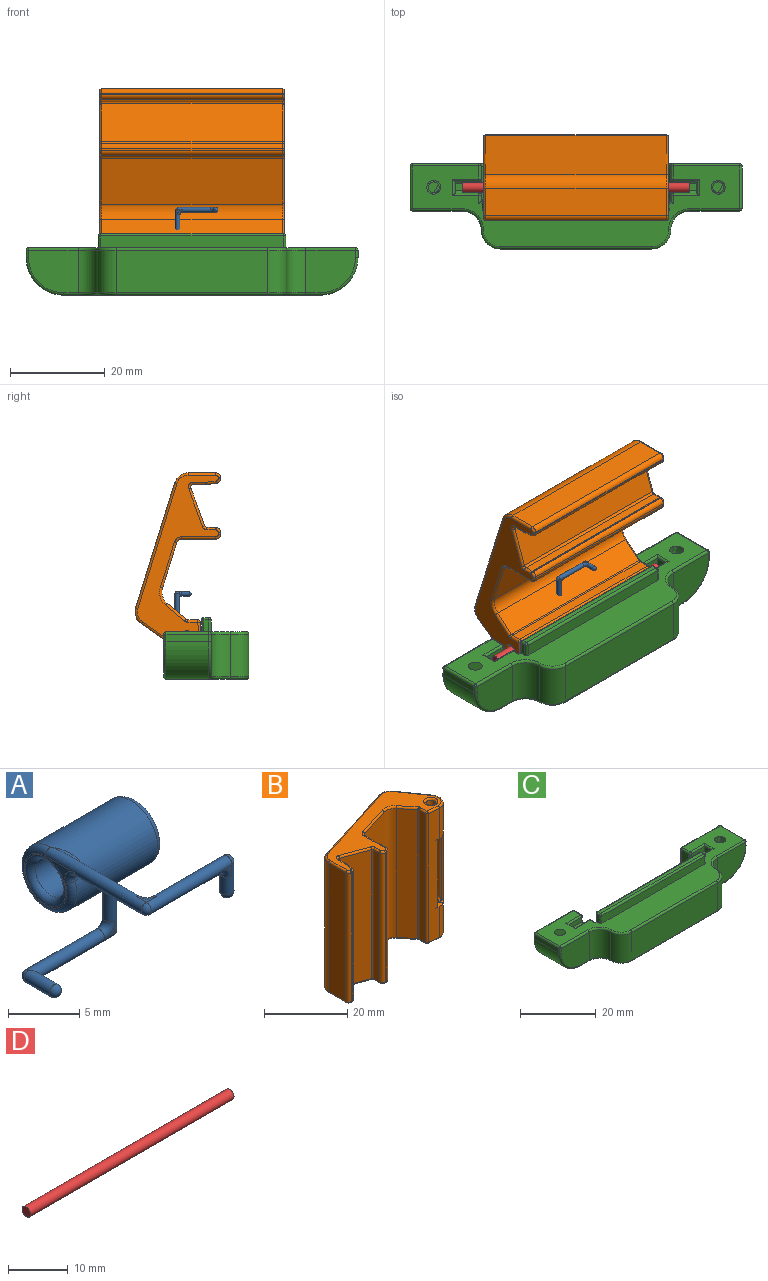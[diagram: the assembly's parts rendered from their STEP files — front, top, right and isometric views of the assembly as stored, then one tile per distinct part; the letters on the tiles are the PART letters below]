
ASSEMBLY  parts=4 mates=3
PART A: 33 faces, bbox 9x12.8x12.8 mm
  f0: plane 1x1mm, normal (0,0,1), area 0.2mm2, adj f12,f14,f16
  f1: plane 1x1mm, normal (0,1,0), area 0.2mm2, adj f24,f27,f29
  f2: plane 1x1mm, normal (0,1,0), area 0.2mm2, adj f16,f19,f20
  f3: cylinder r=2.62mm len=8mm, axis (-1,0,0), area 127.7mm2, adj f10,f11,f21,f22
  f4: cylinder r=1.5mm len=8mm, axis (-1,0,0), area 75.4mm2, adj f31,f32
  f5: plane 5.04x4.25mm, normal (1,0,0), area 2.5mm2, adj f21,f23,f24,f32
  f6: plane 5.04x4.25mm, normal (-1,0,0), area 2.5mm2, adj f11,f12,f13,f31
  f7: plane 1x1mm, normal (0,0,-1), area 0.2mm2, adj f12,f14,f16
  f8: plane 1x1mm, normal (0,-1,0), area 0.2mm2, adj f16,f19,f20
  f9: plane 1x1mm, normal (0,-1,0), area 0.2mm2, adj f24,f27,f29
  f10: bspline ~2.92x1.68mm, area 1.9mm2, adj f3,f12,f13
  f11: torus R=2.12mm, axis (1,0,0), area 9.7mm2, adj f3,f6,f12,f13
  f12: cylinder r=0.5mm len=9.5mm, axis (0,1,0), area 22.9mm2, adj f0,f6,f7,f10,f11,f13,f14,f15
  f13: torus R=1mm, axis (1,0,0), area 1mm2, adj f6,f10,f11,f12
  f14: torus R=1mm, axis (0,0,-1), area 1.7mm2, adj f0,f7,f12,f16
  f15: sphere r=0.5mm, area 0.8mm2, adj f12,f16
  f16: cylinder r=0.5mm len=8mm, axis (1,0,0), area 22mm2, adj f0,f2,f7,f8,f14,f15,f17,f20
  f17: sphere r=0.5mm, area 0.8mm2, adj f16,f19
  f18: sphere r=0.5mm, area 1.6mm2, adj f19
  f19: cylinder r=0.5mm len=2.5mm, axis (0,0,-1), area 6.3mm2, adj f2,f8,f17,f18,f20
  f20: torus R=1mm, axis (0,1,0), area 1.7mm2, adj f2,f8,f16,f19
  f21: torus R=2.12mm, axis (1,0,0), area 9.7mm2, adj f3,f5,f23,f24
  f22: bspline ~2.92x1.68mm, area 1.9mm2, adj f3,f23,f24
  f23: torus R=1mm, axis (1,0,0), area 1mm2, adj f5,f21,f22,f24
  f24: cylinder r=0.5mm len=9.5mm, axis (0,0,-1), area 22.9mm2, adj f1,f5,f9,f21,f22,f23,f26,f27
  f25: sphere r=0.5mm, area 0.8mm2, adj f29,f30
  f26: sphere r=0.5mm, area 0.8mm2, adj f24,f29
  f27: torus R=1mm, axis (0,1,0), area 1.7mm2, adj f1,f9,f24,f29
  f28: sphere r=0.5mm, area 1.6mm2, adj f30
  f29: cylinder r=0.5mm len=8mm, axis (-1,0,0), area 23.1mm2, adj f1,f9,f25,f26,f27,f30
  f30: cylinder r=0.5mm len=2.5mm, axis (0,1,0), area 7.4mm2, adj f25,f28,f29
  f31: torus R=2mm, axis (1,0,0), area 8.3mm2, adj f4,f6
  f32: torus R=2mm, axis (1,0,0), area 8.3mm2, adj f4,f5
PART B: 166 faces, bbox 38.6x18.5x39.2 mm
  f0: plane 19x5.92mm, normal (0.82,0.57,0), area 115.5mm2, adj f27,f32,f34,f35,f37,f39,f40,f42
  f1: plane 9x8.03mm, normal (0.82,0.57,0), area 88.3mm2, adj f3,f4,f30,f117
  f2: cylinder r=1.2mm len=8.5mm, axis (0,0,-1), area 64.1mm2, adj f162,f164
  f3: cylinder r=3mm len=38mm, axis (0,0,-1), area 109.9mm2, adj f1,f5,f6,f27,f30,f31,f63,f83
  f4: cylinder r=3mm len=38mm, axis (0,0,-1), area 212.1mm2, adj f1,f5,f26,f29,f30,f31,f86,f87
  f5: plane 9x8.03mm, normal (0.82,0.57,0), area 88.3mm2, adj f3,f4,f31,f139
  f6: plane 38x26.38mm, normal (-0.3,0.95,0), area 1050mm2, adj f3,f23,f113,f143
  f7: plane 38x5.79mm, normal (-1,0,0), area 220.2mm2, adj f23,f61,f109,f147
  f8: plane 38x0.22mm, normal (0,-1,0), area 8.5mm2, adj f59,f61,f105,f151
  f9: plane 38x2.07mm, normal (0.99,-0.13,0), area 79.2mm2, adj f59,f60,f101,f155
  f10: plane 38x2.72mm, normal (1,0,0), area 103.3mm2, adj f60,f94,f100,f159
  f11: plane 38x8mm, normal (-0.34,-0.94,0), area 323.5mm2, adj f93,f94,f104,f160
  f12: plane 38x1.78mm, normal (-1,0,0), area 67.5mm2, adj f56,f93,f108,f156
  f13: plane 38x0.1mm, normal (-0.98,-0.2,0), area 3.8mm2, adj f56,f57,f112,f152
  f14: plane 38x0.48mm, normal (0,-1,0), area 18.2mm2, adj f57,f58,f116,f148
  f15: plane 38x7.26mm, normal (1,0,0), area 276.1mm2, adj f55,f58,f120,f144
  f16: plane 38x9.6mm, normal (0.3,-0.95,0), area 382mm2, adj f24,f55,f124,f140
  f17: plane 38x4.06mm, normal (-0.77,-0.64,0), area 201.4mm2, adj f24,f128,f132,f136
  f18: plane 38x2.09mm, normal (-1,0,0), area 79.5mm2, adj f92,f127,f131,f132
  f19: cylinder r=1.2mm len=8.5mm, axis (0,0,-1), area 64.1mm2, adj f163,f165
  f20: plane 38x3.51mm, normal (-0.09,-1,0), area 123.7mm2, adj f28,f30,f31,f86,f92,f95,f123,f133
  f21: plane 37x17.03mm, normal (0,0,1), area 195.9mm2, adj f131,f133,f134,f136,f137,f138,f139,f140
  f22: plane 37x17.03mm, normal (0,0,-1), area 195.9mm2, adj f99,f100,f101,f102,f103,f104,f105,f106
  f23: cylinder r=3mm len=38mm, axis (0,0,1), area 144.6mm2, adj f6,f7,f111,f145
  f24: cylinder r=3mm len=38mm, axis (0,0,-1), area 134mm2, adj f16,f17,f126,f138
  f25: cylinder r=2.5mm len=19.5mm, axis (0,0,1), area 76.8mm2, adj f26,f29,f31,f87,f88,f90
  f26: plane 19x0.35mm, normal (-0.71,0.71,0), area 9.5mm2, adj f4,f25,f88,f89
  f27: plane 19x1.2mm, normal (1,-0.08,0), area 23mm2, adj f0,f3,f33,f38,f43,f49,f52,f63
  f28: cylinder r=3mm len=20mm, axis (0,0,1), area 163.3mm2, adj f20,f30,f31,f96,f97,f98
  f29: plane 19x0.35mm, normal (-0.71,-0.71,0), area 9.5mm2, adj f4,f25,f87,f91
  f30: plane 13.71x11.01mm, normal (0,0,1), area 35.3mm2, adj f1,f3,f4,f20,f28,f50,f63,f64
  f31: plane 13.71x11.05mm, normal (0,0,-1), area 37.5mm2, adj f3,f4,f5,f20,f25,f28,f54,f81
  f32: plane 5.53x4.92mm, normal (0,0,1), area 12.5mm2, adj f0,f36,f68,f71
  f33: plane 4.1x2.87mm, normal (0.57,-0.82,0), area 2.5mm2, adj f27,f36,f70,f71
  f34: plane 5.53x4.92mm, normal (0,0,-1), area 12.5mm2, adj f0,f36,f69,f70
  f35: plane 4.1x2.87mm, normal (-0.57,0.82,0), area 2.5mm2, adj f0,f36,f68,f69
  f36: plane 2.87x2.01mm, normal (0.82,0.57,0), area 5mm2, adj f32,f33,f34,f35,f68,f69,f70,f71
  f37: plane 5.53x4.92mm, normal (0,0,1), area 12.5mm2, adj f0,f41,f72,f75
  f38: plane 4.1x2.87mm, normal (0.57,-0.82,0), area 2.5mm2, adj f27,f41,f74,f75
  f39: plane 5.53x4.92mm, normal (0,0,-1), area 12.5mm2, adj f0,f41,f73,f74
  f40: plane 4.1x2.87mm, normal (-0.57,0.82,0), area 2.5mm2, adj f0,f41,f72,f73
  f41: plane 2.87x2.01mm, normal (0.82,0.57,0), area 5mm2, adj f37,f38,f39,f40,f72,f73,f74,f75
  f42: plane 5.53x4.92mm, normal (0,0,1), area 12.5mm2, adj f0,f46,f76,f79
  f43: plane 4.1x2.87mm, normal (0.57,-0.82,0), area 2.5mm2, adj f27,f46,f76,f77
  f44: plane 5.53x4.92mm, normal (0,0,-1), area 12.5mm2, adj f0,f46,f77,f78
  f45: plane 4.1x2.87mm, normal (-0.57,0.82,0), area 2.5mm2, adj f0,f46,f78,f79
  f46: plane 2.87x2.01mm, normal (0.82,0.57,0), area 5mm2, adj f42,f43,f44,f45,f76,f77,f78,f79
  f47: plane 5.53x4.92mm, normal (0,0,-1), area 12.5mm2, adj f0,f50,f62,f67
  f48: plane 4.1x2.87mm, normal (-0.57,0.82,0), area 2.5mm2, adj f0,f50,f66,f67
  f49: plane 4.1x2.87mm, normal (0.57,-0.82,0), area 2.5mm2, adj f27,f50,f62,f64
  f50: plane 2.87x2.01mm, normal (0.82,0.57,0), area 5mm2, adj f30,f47,f48,f49,f62,f64,f66,f67
  f51: plane 5.53x4.92mm, normal (0,0,1), area 12.5mm2, adj f0,f54,f80,f85
  f52: plane 4.1x2.87mm, normal (0.57,-0.82,0), area 2.5mm2, adj f27,f54,f84,f85
  f53: plane 4.1x2.87mm, normal (-0.57,0.82,0), area 2.5mm2, adj f0,f54,f80,f82
  f54: plane 2.87x2.01mm, normal (0.82,0.57,0), area 5mm2, adj f31,f51,f52,f53,f80,f82,f84,f85
  f55: cylinder r=1mm len=38mm, axis (0,0,1), area 48.2mm2, adj f15,f16,f122,f142
  f56: cylinder r=1mm len=38mm, axis (0,0,-1), area 7.5mm2, adj f12,f13,f110,f154
  f57: cylinder r=1mm len=38mm, axis (0,0,-1), area 52.2mm2, adj f13,f14,f114,f150
  f58: cylinder r=1mm len=38mm, axis (0,0,-1), area 59.7mm2, adj f14,f15,f118,f146
  f59: cylinder r=1mm len=38mm, axis (0,0,-1), area 54.7mm2, adj f8,f9,f103,f153
  f60: cylinder r=1mm len=38mm, axis (0,0,1), area 5mm2, adj f9,f10,f99,f157
  f61: cylinder r=1mm len=38mm, axis (0,0,-1), area 59.7mm2, adj f7,f8,f107,f149
  f62: cylinder r=0.5mm len=4.38mm, axis (-0.82,-0.57,0), area 3.9mm2, adj f0,f47,f49,f50
  f63: cylinder r=0.5mm len=1.48mm, axis (-0.08,-1,0), area 1mm2, adj f3,f27,f30,f64
  f64: cylinder r=0.5mm len=4.57mm, axis (0.82,0.57,0), area 4mm2, adj f30,f49,f50,f63
  f65: cylinder r=0.5mm len=4.23mm, axis (0.57,-0.82,0), area 3.4mm2, adj f0,f30,f66,f98
  f66: cylinder r=0.5mm len=4.79mm, axis (0.82,0.57,0), area 4.1mm2, adj f30,f48,f50,f65
  f67: cylinder r=0.5mm len=4.38mm, axis (-0.82,-0.57,0), area 3.9mm2, adj f0,f47,f48,f50
  f68: cylinder r=0.5mm len=4.38mm, axis (0.82,0.57,0), area 3.9mm2, adj f0,f32,f35,f36
  f69: cylinder r=0.5mm len=4.38mm, axis (-0.82,-0.57,0), area 3.9mm2, adj f0,f34,f35,f36
  f70: cylinder r=0.5mm len=4.38mm, axis (-0.82,-0.57,0), area 3.9mm2, adj f0,f33,f34,f36
  f71: cylinder r=0.5mm len=4.38mm, axis (0.82,0.57,0), area 3.9mm2, adj f0,f32,f33,f36
  f72: cylinder r=0.5mm len=4.38mm, axis (0.82,0.57,0), area 3.9mm2, adj f0,f37,f40,f41
  f73: cylinder r=0.5mm len=4.38mm, axis (-0.82,-0.57,0), area 3.9mm2, adj f0,f39,f40,f41
  f74: cylinder r=0.5mm len=4.38mm, axis (-0.82,-0.57,0), area 3.9mm2, adj f0,f38,f39,f41
  f75: cylinder r=0.5mm len=4.38mm, axis (0.82,0.57,0), area 3.9mm2, adj f0,f37,f38,f41
  f76: cylinder r=0.5mm len=4.38mm, axis (0.82,0.57,0), area 3.9mm2, adj f0,f42,f43,f46
  f77: cylinder r=0.5mm len=4.38mm, axis (-0.82,-0.57,0), area 3.9mm2, adj f0,f43,f44,f46
  f78: cylinder r=0.5mm len=4.38mm, axis (-0.82,-0.57,0), area 3.9mm2, adj f0,f44,f45,f46
  f79: cylinder r=0.5mm len=4.38mm, axis (0.82,0.57,0), area 3.9mm2, adj f0,f42,f45,f46
  f80: cylinder r=0.5mm len=4.38mm, axis (0.82,0.57,0), area 3.9mm2, adj f0,f51,f53,f54
  f81: cylinder r=0.5mm len=4.23mm, axis (-0.57,0.82,0), area 3.4mm2, adj f0,f31,f82,f96
  f82: cylinder r=0.5mm len=4.79mm, axis (-0.82,-0.57,0), area 4.1mm2, adj f31,f53,f54,f81
  f83: cylinder r=0.5mm len=1.48mm, axis (0.08,1,0), area 1mm2, adj f3,f27,f31,f84
  f84: cylinder r=0.5mm len=4.57mm, axis (-0.82,-0.57,0), area 4mm2, adj f31,f52,f54,f83
  f85: cylinder r=0.5mm len=4.38mm, axis (0.82,0.57,0), area 3.9mm2, adj f0,f51,f52,f54
  f86: cylinder r=0.5mm len=9mm, axis (0,0,-1), area 0.4mm2, adj f4,f20,f30,f121
  f87: cylinder r=0.5mm len=0.74mm, axis (0.71,-0.71,0), area 0.4mm2, adj f4,f25,f29,f31
  f88: cylinder r=0.5mm len=0.74mm, axis (-0.71,-0.71,0), area 0.4mm2, adj f4,f25,f26,f31
  f89: cylinder r=0.5mm len=1.11mm, axis (0.71,0.71,0), area 0.6mm2, adj f4,f26,f30,f90
  f90: torus R=2mm, axis (0,0,1), area 3.3mm2, adj f25,f30,f89,f91
  f91: cylinder r=0.5mm len=1.11mm, axis (-0.71,0.71,0), area 0.6mm2, adj f4,f29,f30,f90
  f92: cylinder r=0.5mm len=38mm, axis (0,0,-1), area 28.2mm2, adj f18,f20,f125,f130
  f93: cylinder r=0.5mm len=38mm, axis (0,0,1), area 23.2mm2, adj f11,f12,f106,f158
  f94: cylinder r=0.5mm len=38mm, axis (0,0,1), area 36.5mm2, adj f10,f11,f102,f161
  f95: cylinder r=0.5mm len=9mm, axis (0,0,-1), area 0.4mm2, adj f4,f20,f31,f135
  f96: bspline ~1.27x1.21mm, area 0.6mm2, adj f28,f31,f81,f97
  f97: cylinder r=0.5mm len=19mm, axis (0,0,1), area 18.4mm2, adj f0,f28,f96,f98
  f98: bspline ~1.27x1.21mm, area 0.6mm2, adj f28,f30,f65,f97
  f99: torus R=0.5mm, axis (0,0,1), area 0.1mm2, adj f22,f60,f100,f101
  f100: cylinder r=0.5mm len=2.72mm, axis (0,1,0), area 2.1mm2, adj f10,f22,f99,f102
  f101: cylinder r=0.5mm len=2.13mm, axis (0.13,0.99,0), area 1.6mm2, adj f9,f22,f99,f103
  f102: torus R=1mm, axis (0,0,1), area 1mm2, adj f22,f94,f100,f104
  f103: torus R=0.5mm, axis (0,0,1), area 0.9mm2, adj f22,f59,f101,f105
  f104: cylinder r=0.5mm len=8.17mm, axis (0.94,-0.34,0), area 6.7mm2, adj f11,f22,f102,f106
  f105: cylinder r=0.5mm len=0.5mm, axis (1,0,0), area 0.2mm2, adj f8,f22,f103,f107
  f106: torus R=1mm, axis (0,0,1), area 0.7mm2, adj f22,f93,f104,f108
  f107: torus R=0.5mm, axis (0,0,1), area 1mm2, adj f22,f61,f105,f109
  f108: cylinder r=0.5mm len=1.78mm, axis (0,-1,0), area 1.4mm2, adj f12,f22,f106,f110
  f109: cylinder r=0.5mm len=5.79mm, axis (0,-1,0), area 4.6mm2, adj f7,f22,f107,f111
  f110: torus R=0.5mm, axis (0,0,1), area 0.1mm2, adj f22,f56,f108,f112
  f111: torus R=2.5mm, axis (0,0,1), area 2.8mm2, adj f22,f23,f109,f113
  f112: cylinder r=0.5mm len=0.51mm, axis (0.2,-0.98,0), area 0.1mm2, adj f13,f22,f110,f114
  f113: cylinder r=0.5mm len=26.52mm, axis (-0.95,-0.3,0), area 21.7mm2, adj f6,f22,f111,f115
  f114: torus R=0.5mm, axis (0,0,1), area 0.9mm2, adj f22,f57,f112,f116
  f115: torus R=2.5mm, axis (0,0,1), area 2.8mm2, adj f3,f22,f113,f117
  f116: cylinder r=0.5mm len=0.5mm, axis (1,0,0), area 0.4mm2, adj f14,f22,f114,f118
  f117: cylinder r=0.5mm len=8.32mm, axis (-0.57,0.82,0), area 7.7mm2, adj f1,f22,f115,f119
  f118: torus R=0.5mm, axis (0,0,1), area 1mm2, adj f22,f58,f116,f120
  f119: torus R=2.5mm, axis (0,0,1), area 4.8mm2, adj f4,f22,f117,f121
  f120: cylinder r=0.5mm len=7.26mm, axis (0,1,0), area 5.7mm2, adj f15,f22,f118,f122
  f121: sphere r=0.5mm, area 0mm2, adj f86,f119,f123
  f122: torus R=1.5mm, axis (0,0,1), area 1.2mm2, adj f22,f55,f120,f124
  f123: cylinder r=0.5mm len=3.55mm, axis (1,-0.09,0), area 2.8mm2, adj f20,f22,f121,f125
  f124: cylinder r=0.5mm len=9.75mm, axis (0.95,0.3,0), area 7.9mm2, adj f16,f22,f122,f126
  f125: sphere r=0.5mm, area 0.4mm2, adj f92,f123,f127
  f126: torus R=3.5mm, axis (0,0,1), area 2.9mm2, adj f22,f24,f124,f128
  f127: cylinder r=0.5mm len=2.09mm, axis (0,-1,0), area 1.6mm2, adj f18,f22,f125,f129
  f128: cylinder r=0.5mm len=4.38mm, axis (0.64,-0.77,0), area 4.2mm2, adj f17,f22,f126,f129
  f129: torus R=1mm, axis (0,0,1), area 0.4mm2, adj f22,f127,f128,f132
  f130: sphere r=0.5mm, area 0.4mm2, adj f92,f131,f133
  f131: cylinder r=0.5mm len=2.09mm, axis (0,1,0), area 1.6mm2, adj f18,f21,f130,f134
  f132: cylinder r=0.5mm len=38mm, axis (0,0,1), area 13.3mm2, adj f17,f18,f129,f134
  f133: cylinder r=0.5mm len=3.55mm, axis (-1,0.09,0), area 2.8mm2, adj f20,f21,f130,f135
  f134: torus R=1mm, axis (0,0,1), area 0.4mm2, adj f21,f131,f132,f136
  f135: sphere r=0.5mm, area 0mm2, adj f95,f133,f137
  f136: cylinder r=0.5mm len=4.38mm, axis (-0.64,0.77,0), area 4.2mm2, adj f17,f21,f134,f138
  f137: torus R=2.5mm, axis (0,0,1), area 4.8mm2, adj f4,f21,f135,f139
  f138: torus R=3.5mm, axis (0,0,1), area 2.9mm2, adj f21,f24,f136,f140
  f139: cylinder r=0.5mm len=8.32mm, axis (0.57,-0.82,0), area 7.7mm2, adj f5,f21,f137,f141
  f140: cylinder r=0.5mm len=9.75mm, axis (-0.95,-0.3,0), area 7.9mm2, adj f16,f21,f138,f142
  f141: torus R=2.5mm, axis (0,0,1), area 2.8mm2, adj f3,f21,f139,f143
  f142: torus R=1.5mm, axis (0,0,1), area 1.2mm2, adj f21,f55,f140,f144
  f143: cylinder r=0.5mm len=26.52mm, axis (0.95,0.3,0), area 21.7mm2, adj f6,f21,f141,f145
  f144: cylinder r=0.5mm len=7.26mm, axis (0,-1,0), area 5.7mm2, adj f15,f21,f142,f146
  f145: torus R=2.5mm, axis (0,0,1), area 2.8mm2, adj f21,f23,f143,f147
  f146: torus R=0.5mm, axis (0,0,1), area 1mm2, adj f21,f58,f144,f148
  f147: cylinder r=0.5mm len=5.79mm, axis (0,1,0), area 4.6mm2, adj f7,f21,f145,f149
  f148: cylinder r=0.5mm len=0.5mm, axis (-1,0,0), area 0.4mm2, adj f14,f21,f146,f150
  f149: torus R=0.5mm, axis (0,0,1), area 1mm2, adj f21,f61,f147,f151
  f150: torus R=0.5mm, axis (0,0,1), area 0.9mm2, adj f21,f57,f148,f152
  f151: cylinder r=0.5mm len=0.5mm, axis (-1,0,0), area 0.2mm2, adj f8,f21,f149,f153
  f152: cylinder r=0.5mm len=0.51mm, axis (-0.2,0.98,0), area 0.1mm2, adj f13,f21,f150,f154
  f153: torus R=0.5mm, axis (0,0,1), area 0.9mm2, adj f21,f59,f151,f155
  f154: torus R=0.5mm, axis (0,0,1), area 0.1mm2, adj f21,f56,f152,f156
  f155: cylinder r=0.5mm len=2.13mm, axis (-0.13,-0.99,0), area 1.6mm2, adj f9,f21,f153,f157
  f156: cylinder r=0.5mm len=1.78mm, axis (0,1,0), area 1.4mm2, adj f12,f21,f154,f158
  f157: torus R=0.5mm, axis (0,0,1), area 0.1mm2, adj f21,f60,f155,f159
  f158: torus R=1mm, axis (0,0,1), area 0.7mm2, adj f21,f93,f156,f160
  f159: cylinder r=0.5mm len=2.72mm, axis (0,-1,0), area 2.1mm2, adj f10,f21,f157,f161
  f160: cylinder r=0.5mm len=8.17mm, axis (-0.94,0.34,0), area 6.7mm2, adj f11,f21,f158,f161
  f161: torus R=1mm, axis (0,0,1), area 1mm2, adj f21,f94,f159,f160
  f162: torus R=1.7mm, axis (0,0,1), area 6.8mm2, adj f2,f30
  f163: torus R=1.7mm, axis (0,0,1), area 6.8mm2, adj f19,f31
  f164: torus R=1.7mm, axis (0,0,1), area 6.8mm2, adj f2,f22
  f165: torus R=1.7mm, axis (0,0,1), area 6.8mm2, adj f19,f21
PART C: 143 faces, bbox 71.3x18.3x13.7 mm
  f0: plane 40x8.5mm, normal (0,1,0), area 167.2mm2, adj f17,f18,f39,f40,f49,f52,f53,f54
  f1: plane 69x17mm, normal (0,0,1), area 497.6mm2, adj f20,f21,f22,f24,f26,f42,f43,f54
  f2: plane 69x9mm, normal (0,1,0), area 271.5mm2, adj f80,f81,f84,f85,f88,f89,f90,f93
  f3: plane 5x1.5mm, normal (0,-1,0), area 7.5mm2, adj f12,f70,f78,f79
  f4: plane 5x1.5mm, normal (0,1,0), area 7.5mm2, adj f12,f59,f61,f69
  f5: plane 5x1.5mm, normal (0,0,1), area 7.5mm2, adj f12,f59,f70,f71
  f6: plane 10.5x9mm, normal (0,-1,0), area 82.4mm2, adj f35,f102,f104,f106,f141
  f7: plane 32x9mm, normal (0,-1,0), area 288mm2, adj f34,f37,f112,f138
  f8: plane 10.5x9mm, normal (0,-1,0), area 82.4mm2, adj f36,f103,f105,f107,f135
  f9: plane 9x1.5mm, normal (1,0,0), area 13.5mm2, adj f33,f97,f101,f103
  f10: plane 9x1.5mm, normal (-1,0,0), area 13.5mm2, adj f32,f94,f100,f102
  f11: plane 54x17mm, normal (0,0,-1), area 801.4mm2, adj f32,f33,f89,f106,f107,f108,f109,f110
  f12: plane 2.5x2mm, normal (-1,0,0), area 4.9mm2, adj f3,f4,f5,f59,f70,f74
  f13: plane 5x1.5mm, normal (0,-1,0), area 7.5mm2, adj f14,f67,f76,f77
  f14: plane 2.5x2mm, normal (1,0,0), area 4.9mm2, adj f13,f15,f16,f55,f67,f73
  f15: plane 5x1.5mm, normal (0,1,0), area 7.5mm2, adj f14,f55,f57,f68
  f16: plane 5x1.5mm, normal (0,0,1), area 7.5mm2, adj f14,f55,f66,f67
  f17: plane 7.5x5.5mm, normal (-1,0,0), area 32.9mm2, adj f0,f38,f60,f61,f65,f71,f75,f79
  f18: plane 7.5x5.5mm, normal (1,0,0), area 32.9mm2, adj f0,f41,f57,f58,f62,f66,f72,f76
  f19: plane 36x15mm, normal (0,0,1), area 474.9mm2, adj f38,f39,f40,f41,f80,f113,f117,f125
  f20: plane 38.5x2.5mm, normal (0,-1,0), area 96.2mm2, adj f1,f42,f43,f44
  f21: plane 2.5x1mm, normal (1,0,0), area 2.5mm2, adj f1,f43,f48,f53
  f22: plane 2.5x1mm, normal (-1,0,0), area 2.5mm2, adj f1,f42,f47,f52
  f23: plane 38.5x1mm, normal (0,0,1), area 38.5mm2, adj f44,f47,f48,f49
  f24: cone r=1.45mm half-angle=2.5deg, axis (0,0,1), area 57.1mm2, adj f1,f25
  f25: plane 2.29x2.29mm, normal (0,0,1), area 4.1mm2, adj f24
  f26: cone r=1.45mm half-angle=2.5deg, axis (0,0,1), area 57.1mm2, adj f1,f27
  f27: plane 2.29x2.29mm, normal (0,0,1), area 4.1mm2, adj f26
  f28: plane 7.5x5.93mm, normal (1,0,0), area 38.7mm2, adj f114,f116,f117,f118,f119
  f29: plane 7.5x5.93mm, normal (-1,0,0), area 38.7mm2, adj f124,f127,f130,f131,f133
  f30: plane 29x5.06mm, normal (0,1,0), area 146.7mm2, adj f116,f120,f124,f125
  f31: plane 29x7.12mm, normal (0,0.12,-0.99), area 208.2mm2, adj f119,f120,f126,f127
  f32: cylinder r=8mm len=9mm, axis (0,1,0), area 113.1mm2, adj f10,f11,f90,f104
  f33: cylinder r=8mm len=9mm, axis (0,-1,0), area 113.1mm2, adj f9,f11,f93,f105
  f34: cylinder r=4mm len=9mm, axis (0,0,1), area 56.5mm2, adj f7,f35,f110,f139
  f35: cylinder r=4mm len=9mm, axis (0,0,1), area 56.5mm2, adj f6,f34,f108,f140
  f36: cylinder r=4mm len=9mm, axis (0,0,1), area 56.5mm2, adj f8,f37,f109,f136
  f37: cylinder r=4mm len=9mm, axis (0,0,1), area 56.5mm2, adj f7,f36,f111,f137
  f38: cylinder r=2mm len=7.5mm, axis (0,1,0), area 21.3mm2, adj f17,f19,f39,f84
  f39: cylinder r=2mm len=4.5mm, axis (1,0,0), area 11.9mm2, adj f0,f19,f38,f133
  f40: cylinder r=2mm len=4.5mm, axis (1,0,0), area 11.9mm2, adj f0,f19,f41,f114
  f41: cylinder r=2mm len=7.5mm, axis (0,-1,0), area 21.3mm2, adj f18,f19,f40,f81
  f42: cylinder r=0.5mm len=2.5mm, axis (0,0,1), area 2mm2, adj f1,f20,f22,f45
  f43: cylinder r=0.5mm len=2.5mm, axis (0,0,-1), area 2mm2, adj f1,f20,f21,f46
  f44: cylinder r=0.5mm len=38.5mm, axis (-1,0,0), area 30.2mm2, adj f20,f23,f45,f46
  f45: sphere r=0.5mm, area 0.4mm2, adj f42,f44,f47
  f46: sphere r=0.5mm, area 0.4mm2, adj f43,f44,f48
  f47: cylinder r=0.5mm len=1mm, axis (0,1,0), area 0.8mm2, adj f22,f23,f45,f50
  f48: cylinder r=0.5mm len=1mm, axis (0,-1,0), area 0.8mm2, adj f21,f23,f46,f51
  f49: cylinder r=0.5mm len=38.5mm, axis (-1,0,0), area 30.2mm2, adj f0,f23,f50,f51
  f50: sphere r=0.5mm, area 0.4mm2, adj f47,f49,f52
  f51: sphere r=0.5mm, area 0.4mm2, adj f48,f49,f53
  f52: cylinder r=0.5mm len=3mm, axis (0,0,-1), area 2.1mm2, adj f0,f22,f50,f54
  f53: cylinder r=0.5mm len=3mm, axis (0,0,1), area 2.1mm2, adj f0,f21,f51,f56
  f54: cylinder r=0.5mm len=1.25mm, axis (-1,0,0), area 0.5mm2, adj f0,f1,f52,f58
  f55: cylinder r=0.5mm len=5mm, axis (1,0,0), area 3.9mm2, adj f14,f15,f16,f62
  f56: cylinder r=0.5mm len=1.25mm, axis (-1,0,0), area 0.5mm2, adj f0,f1,f53,f60
  f57: cylinder r=0.5mm len=1.5mm, axis (0,0,-1), area 1.2mm2, adj f15,f18,f62,f63
  f58: cylinder r=0.5mm len=1.75mm, axis (0,1,0), area 1.1mm2, adj f1,f18,f54,f63
  f59: cylinder r=0.5mm len=5mm, axis (1,0,0), area 3.9mm2, adj f4,f5,f12,f65
  f60: cylinder r=0.5mm len=1.75mm, axis (0,-1,0), area 1.1mm2, adj f1,f17,f56,f64
  f61: cylinder r=0.5mm len=1.5mm, axis (0,0,1), area 1.2mm2, adj f4,f17,f64,f65
  f62: torus R=1mm, axis (-1,0,0), area 0.8mm2, adj f18,f55,f57,f66
  f63: sphere r=0.5mm, area 0.4mm2, adj f57,f58,f68
  f64: sphere r=0.5mm, area 0.4mm2, adj f60,f61,f69
  f65: torus R=1mm, axis (-1,0,0), area 0.8mm2, adj f17,f59,f61,f71
  f66: cylinder r=0.5mm len=1.5mm, axis (0,1,0), area 1.2mm2, adj f16,f18,f62,f72
  f67: cylinder r=0.5mm len=5mm, axis (-1,0,0), area 3.9mm2, adj f13,f14,f16,f72
  f68: cylinder r=0.5mm len=5.5mm, axis (-1,0,0), area 4.1mm2, adj f1,f15,f63,f73
  f69: cylinder r=0.5mm len=5.5mm, axis (-1,0,0), area 4.1mm2, adj f1,f4,f64,f74
  f70: cylinder r=0.5mm len=5mm, axis (-1,0,0), area 3.9mm2, adj f3,f5,f12,f75
  f71: cylinder r=0.5mm len=1.5mm, axis (0,-1,0), area 1.2mm2, adj f5,f17,f65,f75
  f72: torus R=1mm, axis (-1,0,0), area 0.8mm2, adj f18,f66,f67,f76
  f73: cylinder r=0.5mm len=3.5mm, axis (0,1,0), area 2.2mm2, adj f1,f14,f68,f77
  f74: cylinder r=0.5mm len=3.5mm, axis (0,-1,0), area 2.2mm2, adj f1,f12,f69,f78
  f75: torus R=1mm, axis (-1,0,0), area 0.8mm2, adj f17,f70,f71,f79
  f76: cylinder r=0.5mm len=1.5mm, axis (0,0,1), area 1.2mm2, adj f13,f18,f72,f82
  f77: cylinder r=0.5mm len=5.5mm, axis (1,0,0), area 4.1mm2, adj f1,f13,f73,f82
  f78: cylinder r=0.5mm len=5.5mm, axis (1,0,0), area 4.1mm2, adj f1,f3,f74,f83
  f79: cylinder r=0.5mm len=1.5mm, axis (0,0,-1), area 1.2mm2, adj f3,f17,f75,f83
  f80: cylinder r=0.5mm len=36mm, axis (-1,0,0), area 28.3mm2, adj f2,f19,f81,f84
  f81: torus R=2.5mm, axis (0,1,0), area 2.7mm2, adj f2,f41,f80,f85
  f82: sphere r=0.5mm, area 0.4mm2, adj f76,f77,f86
  f83: sphere r=0.5mm, area 0.4mm2, adj f78,f79,f87
  f84: torus R=2.5mm, axis (0,1,0), area 2.7mm2, adj f2,f38,f80,f88
  f85: cylinder r=0.5mm len=5.5mm, axis (0,0,-1), area 4.3mm2, adj f2,f18,f81,f91
  f86: cylinder r=0.5mm len=2.75mm, axis (0,1,0), area 2.2mm2, adj f1,f18,f82,f91
  f87: cylinder r=0.5mm len=2.75mm, axis (0,-1,0), area 2.2mm2, adj f1,f17,f83,f92
  f88: cylinder r=0.5mm len=5.5mm, axis (0,0,1), area 4.3mm2, adj f2,f17,f84,f92
  f89: cylinder r=0.5mm len=54mm, axis (1,0,0), area 42.4mm2, adj f2,f11,f90,f93
  f90: torus R=7.5mm, axis (0,1,0), area 9.6mm2, adj f2,f32,f89,f94
  f91: sphere r=0.5mm, area 0.4mm2, adj f85,f86,f95
  f92: sphere r=0.5mm, area 0.4mm2, adj f87,f88,f96
  f93: torus R=7.5mm, axis (0,1,0), area 9.6mm2, adj f2,f33,f89,f97
  f94: cylinder r=0.5mm len=1.5mm, axis (0,0,-1), area 1.2mm2, adj f2,f10,f90,f98
  f95: cylinder r=0.5mm len=14mm, axis (-1,0,0), area 11mm2, adj f1,f2,f91,f98
  f96: cylinder r=0.5mm len=14mm, axis (-1,0,0), area 11mm2, adj f1,f2,f92,f99
  f97: cylinder r=0.5mm len=1.5mm, axis (0,0,1), area 1.2mm2, adj f2,f9,f93,f99
  f98: sphere r=0.5mm, area 0.4mm2, adj f94,f95,f100
  f99: sphere r=0.5mm, area 0.4mm2, adj f96,f97,f101
  f100: cylinder r=0.5mm len=9mm, axis (0,-1,0), area 7.1mm2, adj f1,f10,f98,f142
  f101: cylinder r=0.5mm len=9mm, axis (0,1,0), area 7.1mm2, adj f1,f9,f99,f134
  f102: cylinder r=0.5mm len=1.5mm, axis (0,0,1), area 1.2mm2, adj f6,f10,f104,f142
  f103: cylinder r=0.5mm len=1.5mm, axis (0,0,-1), area 1.2mm2, adj f8,f9,f105,f134
  f104: torus R=7.5mm, axis (0,1,0), area 9.6mm2, adj f6,f32,f102,f106
  f105: torus R=7.5mm, axis (0,1,0), area 9.6mm2, adj f8,f33,f103,f107
  f106: cylinder r=0.5mm len=3mm, axis (-1,0,0), area 2.4mm2, adj f6,f11,f104,f108
  f107: cylinder r=0.5mm len=3mm, axis (-1,0,0), area 2.4mm2, adj f8,f11,f105,f109
  f108: torus R=4.5mm, axis (0,0,1), area 5.2mm2, adj f11,f35,f106,f110
  f109: torus R=4.5mm, axis (0,0,1), area 5.2mm2, adj f11,f36,f107,f111
  f110: torus R=3.5mm, axis (0,0,1), area 4.7mm2, adj f11,f34,f108,f112
  f111: torus R=3.5mm, axis (0,0,1), area 4.7mm2, adj f11,f37,f109,f112
  f112: cylinder r=0.5mm len=32mm, axis (-1,0,0), area 25.1mm2, adj f7,f11,f110,f111
  f113: bspline ~2.34x1mm, area 0.9mm2, adj f19,f114,f117
  f114: torus R=2.5mm, axis (-1,0,0), area 1.7mm2, adj f28,f40,f113,f118
  f115: sphere r=0.5mm, area 0.4mm2, adj f116,f119,f120
  f116: cylinder r=0.5mm len=5.06mm, axis (0,0,1), area 4mm2, adj f28,f30,f115,f121
  f117: cylinder r=0.5mm len=7.5mm, axis (0,1,0), area 5.9mm2, adj f19,f28,f113,f121
  f118: cylinder r=0.5mm len=4.43mm, axis (0,0,1), area 3.5mm2, adj f0,f28,f114,f122
  f119: cylinder r=0.5mm len=7.19mm, axis (0,0.99,0.12), area 5.6mm2, adj f28,f31,f115,f122
  f120: cylinder r=0.5mm len=29mm, axis (1,0,0), area 21mm2, adj f30,f31,f115,f123
  f121: sphere r=0.5mm, area 0.4mm2, adj f116,f117,f125
  f122: bspline ~1.18x1mm, area 0.8mm2, adj f0,f118,f119,f126
  f123: sphere r=0.5mm, area 0.4mm2, adj f120,f124,f127
  f124: cylinder r=0.5mm len=5.06mm, axis (0,0,-1), area 4mm2, adj f29,f30,f123,f128
  f125: cylinder r=0.5mm len=29mm, axis (-1,0,0), area 22.8mm2, adj f19,f30,f121,f128
  f126: cylinder r=0.5mm len=29mm, axis (1,0,0), area 21mm2, adj f0,f31,f122,f129
  f127: cylinder r=0.5mm len=7.19mm, axis (0,0.99,0.12), area 5.6mm2, adj f29,f31,f123,f129
  f128: sphere r=0.5mm, area 0.4mm2, adj f124,f125,f130
  f129: bspline ~1.18x1mm, area 0.8mm2, adj f0,f126,f127,f131
  f130: cylinder r=0.5mm len=7.5mm, axis (0,-1,0), area 5.9mm2, adj f19,f29,f128,f132
  f131: cylinder r=0.5mm len=4.43mm, axis (0,0,-1), area 3.5mm2, adj f0,f29,f129,f133
  f132: bspline ~2.34x1mm, area 0.9mm2, adj f19,f130,f133
  f133: torus R=2.5mm, axis (-1,0,0), area 1.7mm2, adj f29,f39,f131,f132
  f134: sphere r=0.5mm, area 0.4mm2, adj f101,f103,f135
  f135: cylinder r=0.5mm len=10.5mm, axis (1,0,0), area 8.2mm2, adj f1,f8,f134,f136
  f136: torus R=4.5mm, axis (0,0,1), area 5.2mm2, adj f1,f36,f135,f137
  f137: torus R=3.5mm, axis (0,0,1), area 4.7mm2, adj f1,f37,f136,f138
  f138: cylinder r=0.5mm len=32mm, axis (1,0,0), area 25.1mm2, adj f1,f7,f137,f139
  f139: torus R=3.5mm, axis (0,0,1), area 4.7mm2, adj f1,f34,f138,f140
  f140: torus R=4.5mm, axis (0,0,1), area 5.2mm2, adj f1,f35,f139,f141
  f141: cylinder r=0.5mm len=10.5mm, axis (1,0,0), area 8.2mm2, adj f1,f6,f140,f142
  f142: sphere r=0.5mm, area 0.4mm2, adj f100,f102,f141
PART D: 3 faces, bbox 48x2x2 mm
  f0: cylinder r=1mm len=48mm, axis (-1,0,0), area 301.6mm2, adj f1,f2
  f1: plane 2x2mm, normal (1,0,0), area 3.1mm2, adj f0
  f2: plane 2x2mm, normal (-1,0,0), area 3.1mm2, adj f0
PLACE A rot(axis=(-1,0,0),90deg) t=(-5.62,-5.95,-7.21)mm
PLACE B rot(axis=(0,1,0),90deg) t=(-2.09,-5.95,-7.21)mm
PLACE C rot(axis=(-1,0,0),0deg) t=(-2.09,-6.45,-0.23)mm
PLACE D rot(axis=(1,-0.06,0.06),0deg) t=(-2.09,-5.95,-7.21)mm
MATE fastened D.f0 <-> C.f14  axis (-1,0,0) through (-27.59,-5.95,-7.21)mm
MATE cylindrical B.f2 <-> D.f0  axis (-1,0,0) through (16.91,-5.95,-7.21)mm
MATE cylindrical A.f4 <-> D.f0  axis (-1,0,0) through (2.88,-5.95,-7.21)mm
